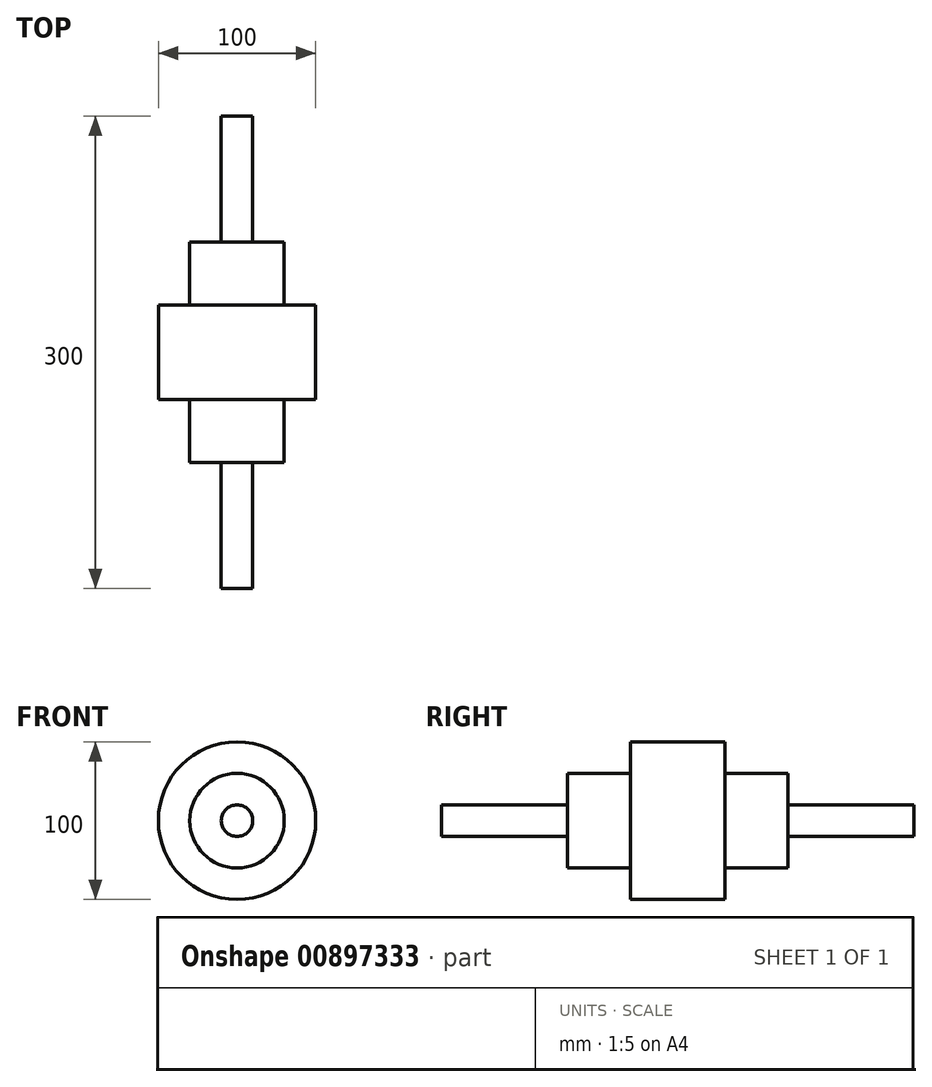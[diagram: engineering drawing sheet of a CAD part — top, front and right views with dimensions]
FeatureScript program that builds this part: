
annotation { "Feature Type Name" : "Feature", "Feature Type Description" : "" }
export const myFeature = defineFeature(function(context is Context, id is Id, definition is map)
    precondition{}
    {
        {
            var Q0;
            Q0=qCreatedBy(makeId("Front.planeOp"),FACE);
            var sketch = newSketch(context, id + "F0", { "sketchPlane" : qUnion([Q0])});
            skCircle(sketch, "E0", {"center": v(0, 0) * mm, "radius": 50 * mm});
            skSolve(sketch);
        }
        {
            var Q0;
            Q0=makeQuery(id+"F0.imprint","IMPRINT",FACE,{"disambiguationData":[TD([[makeQuery(id+"F0.imprint","IMPRINT",EDGE,{"derivedFrom":sQuery(id+"F0.wireOp",EDGE,"E0")}),1.0]])]});
            var Q1;
            Q1=sQuery(id+"F0.wireOp",EDGE,"E0");
            extrude(context, id + "F1", {"entities" : qUnion([Q0]), "surfaceEntities" : qUnion([Q1]), "depth" : 30 * mm, "offsetDistance" : 25.4 * mm});
        }
        {
            var Q0;
            Q0=qCreatedBy(makeId("Front.planeOp"),FACE);
            var sketch = newSketch(context, id + "F2", { "sketchPlane" : qUnion([Q0])});
            skCircle(sketch, "E1", {"center": v(0, 0) * mm, "radius": 50 * mm});
            skSolve(sketch);
        }
        {
            var Q0;
            Q0=makeQuery(id+"F2.imprint","IMPRINT",FACE,{"disambiguationData":[TD([[makeQuery(id+"F2.imprint","IMPRINT",EDGE,{"derivedFrom":sQuery(id+"F2.wireOp",EDGE,"E1")}),1.0]])]});
            var Q1;
            Q1=sQuery(id+"F2.wireOp",EDGE,"E1");
            extrude(context, id + "F3", {"entities" : qUnion([Q0]), "operationType" : NewBodyOperationType.ADD, "surfaceEntities" : qUnion([Q1]), "oppositeDirection" : true, "depth" : 30 * mm, "offsetDistance" : 25.4 * mm});
        }
        {
            var Q0;
            Q0=makeQuery(id+"F1.opExtrude","CAP_FACE",FACE,{"disambiguationData":[OSD([sQuery(id+"F0.wireOp",EDGE,"E0")])],"isStart":false});
            var sketch = newSketch(context, id + "F4", { "sketchPlane" : qUnion([Q0])});
            skCircle(sketch, "E2", {"center": v(0, 0) * mm, "radius": 30 * mm});
            skSolve(sketch);
        }
        {
            var Q0;
            Q0=makeQuery(id+"F4.imprint","IMPRINT",FACE,{"disambiguationData":[TD([[makeQuery(id+"F4.imprint","IMPRINT",EDGE,{"derivedFrom":sQuery(id+"F4.wireOp",EDGE,"E2")}),1.0]])]});
            var Q1;
            Q1=sQuery(id+"F4.wireOp",EDGE,"E2");
            extrude(context, id + "F5", {"entities" : qUnion([Q0]), "operationType" : NewBodyOperationType.ADD, "surfaceEntities" : qUnion([Q1]), "depth" : 40 * mm, "offsetDistance" : 25.4 * mm});
        }
        {
            var Q0;
            Q0=makeQuery(id+"F3.opExtrude","CAP_FACE",FACE,{"disambiguationData":[OSD([sQuery(id+"F2.wireOp",EDGE,"E1")])],"isStart":false});
            var sketch = newSketch(context, id + "F6", { "sketchPlane" : qUnion([Q0])});
            skCircle(sketch, "E3", {"center": v(0, 0) * mm, "radius": 30 * mm});
            skSolve(sketch);
        }
        {
            var Q0;
            Q0=makeQuery(id+"F6.imprint","IMPRINT",FACE,{"disambiguationData":[TD([[makeQuery(id+"F6.imprint","IMPRINT",EDGE,{"derivedFrom":sQuery(id+"F6.wireOp",EDGE,"E3")}),1.0]])]});
            var Q1;
            Q1=sQuery(id+"F6.wireOp",EDGE,"E3");
            extrude(context, id + "F7", {"entities" : qUnion([Q0]), "operationType" : NewBodyOperationType.ADD, "surfaceEntities" : qUnion([Q1]), "depth" : 40 * mm, "offsetDistance" : 25.4 * mm});
        }
        {
            var Q0;
            Q0=makeQuery(id+"F5.opExtrude","CAP_FACE",FACE,{"disambiguationData":[OSD([sQuery(id+"F4.wireOp",EDGE,"E2")])],"isStart":false});
            var sketch = newSketch(context, id + "F8", { "sketchPlane" : qUnion([Q0])});
            skCircle(sketch, "E4", {"center": v(0, 0) * mm, "radius": 10 * mm});
            skSolve(sketch);
        }
        {
            var Q0;
            Q0=makeQuery(id+"F8.imprint","IMPRINT",FACE,{"disambiguationData":[TD([[makeQuery(id+"F8.imprint","IMPRINT",EDGE,{"derivedFrom":sQuery(id+"F8.wireOp",EDGE,"E4")}),1.0]])]});
            var Q1;
            Q1=sQuery(id+"F8.wireOp",EDGE,"E4");
            extrude(context, id + "F9", {"entities" : qUnion([Q0]), "operationType" : NewBodyOperationType.ADD, "surfaceEntities" : qUnion([Q1]), "depth" : 80 * mm, "offsetDistance" : 25.4 * mm});
        }
        {
            var Q0;
            Q0=makeQuery(id+"F7.opExtrude","CAP_FACE",FACE,{"disambiguationData":[OSD([sQuery(id+"F6.wireOp",EDGE,"E3")])],"isStart":false});
            var sketch = newSketch(context, id + "F10", { "sketchPlane" : qUnion([Q0])});
            skCircle(sketch, "E5", {"center": v(0, 0) * mm, "radius": 10 * mm});
            skSolve(sketch);
        }
        {
            var Q0;
            Q0=makeQuery(id+"F10.imprint","IMPRINT",FACE,{"disambiguationData":[TD([[makeQuery(id+"F10.imprint","IMPRINT",EDGE,{"derivedFrom":sQuery(id+"F10.wireOp",EDGE,"E5")}),1.0]])]});
            var Q1;
            Q1=sQuery(id+"F10.wireOp",EDGE,"E5");
            extrude(context, id + "F11", {"entities" : qUnion([Q0]), "operationType" : NewBodyOperationType.ADD, "surfaceEntities" : qUnion([Q1]), "depth" : 80 * mm, "offsetDistance" : 25.4 * mm});
        }
    });
